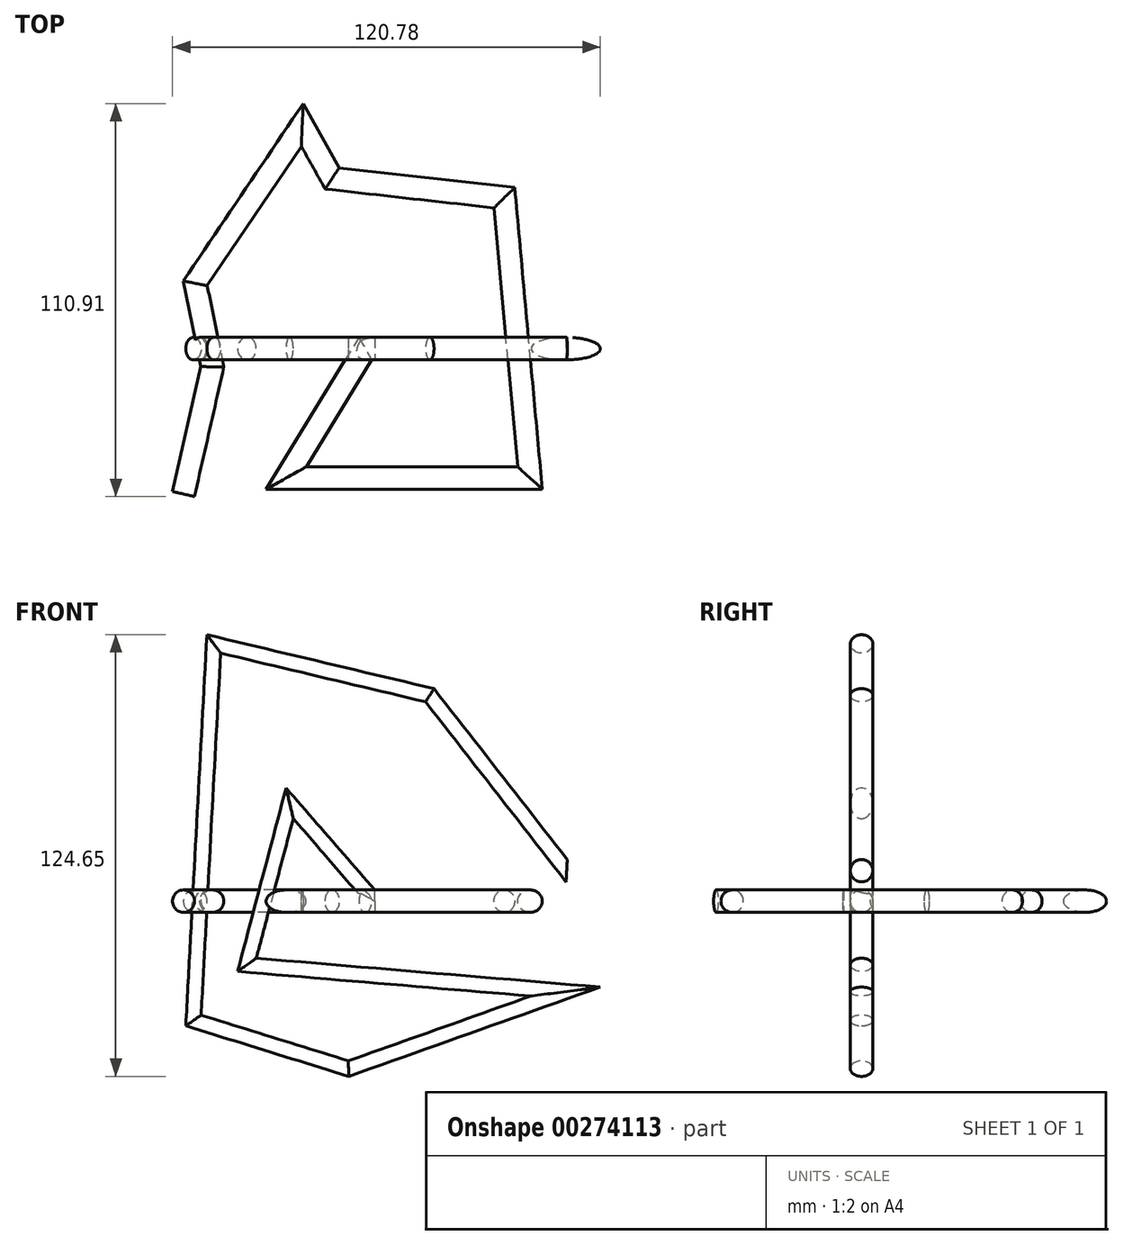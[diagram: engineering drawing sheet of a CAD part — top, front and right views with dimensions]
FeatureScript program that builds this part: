
annotation { "Feature Type Name" : "Feature", "Feature Type Description" : "" }
export const myFeature = defineFeature(function(context is Context, id is Id, definition is map)
    precondition{}
    {
        {
            var Q0;
            Q0=qCreatedBy(makeId("Top.planeOp"),FACE);
            var sketch = newSketch(context, id + "F0", { "sketchPlane" : qUnion([Q0])});
            skLineSegment(sketch, "E0", {"start": v(-2.66, 0) * mm, "end": v(-25, -36.52) * mm});
            skLineSegment(sketch, "E1", {"start": v(-25, -36.52) * mm, "end": v(43.84, -36.52) * mm});
            skLineSegment(sketch, "E2", {"start": v(43.84, -36.52) * mm, "end": v(36.6, 42.58) * mm});
            skLineSegment(sketch, "E3", {"start": v(36.6, 42.58) * mm, "end": v(-12.02, 48.02) * mm});
            skLineSegment(sketch, "E4", {"start": v(-12.02, 48.02) * mm, "end": v(-20.47, 63.11) * mm});
            skLineSegment(sketch, "E5", {"start": v(-20.47, 63.11) * mm, "end": v(-50.66, 18.43) * mm});
            skLineSegment(sketch, "E6", {"start": v(-50.66, 18.43) * mm, "end": v(-45.83, -5.12) * mm});
            skLineSegment(sketch, "E7", {"start": v(-45.83, -5.12) * mm, "end": v(-53.99, -41.05) * mm});
            skLineSegment(sketch, "E8", {"start": v(-2.66, 0) * mm, "end": v(0, 0) * mm});
            skSolve(sketch);
        }
        {
            var Q0;
            Q0=qCreatedBy(makeId("Front.planeOp"),FACE);
            var sketch = newSketch(context, id + "F1", { "sketchPlane" : qUnion([Q0])});
            skLineSegment(sketch, "E9", {"start": v(0, 0) * mm, "end": v(-24, 27.63) * mm});
            skLineSegment(sketch, "E10", {"start": v(-24, 27.63) * mm, "end": v(-36.08, -17.96) * mm});
            skLineSegment(sketch, "E11", {"start": v(-36.08, -17.96) * mm, "end": v(53.9, -25.51) * mm});
            skLineSegment(sketch, "E12", {"start": v(53.9, -25.51) * mm, "end": v(-7.4, -47.25) * mm});
            skLineSegment(sketch, "E13", {"start": v(-7.4, -47.25) * mm, "end": v(-51.18, -33.66) * mm});
            skLineSegment(sketch, "E14", {"start": v(-51.18, -33.66) * mm, "end": v(-45.44, 72.61) * mm});
            skLineSegment(sketch, "E15", {"start": v(-45.44, 72.61) * mm, "end": v(15.55, 58.12) * mm});
            skLineSegment(sketch, "E16", {"start": v(15.55, 58.12) * mm, "end": v(54.2, 8.6) * mm});
            skSolve(sketch);
        }
        {
            var Q0;
            Q0=qCreatedBy(makeId("Right.planeOp"),FACE);
            var sketch = newSketch(context, id + "F2", { "sketchPlane" : qUnion([Q0])});
            skCircle(sketch, "E17", {"center": v(0, 0) * mm, "radius": 3.18 * mm});
            skSolve(sketch);
        }
        {
            var Q0;
            Q0=makeQuery(id+"F2.imprint","IMPRINT",FACE,{"disambiguationData":[TD([[makeQuery(id+"F2.imprint","IMPRINT",EDGE,{"derivedFrom":sQuery(id+"F2.wireOp",EDGE,"E17")}),1.0]])]});
            var Q1;
            Q1=sQuery(id+"F1.wireOp",EDGE,"E9");
            var Q2;
            Q2=sQuery(id+"F1.wireOp",EDGE,"E10");
            var Q3;
            Q3=sQuery(id+"F1.wireOp",EDGE,"E11");
            var Q4;
            Q4=sQuery(id+"F1.wireOp",EDGE,"E12");
            var Q5;
            Q5=sQuery(id+"F1.wireOp",EDGE,"E13");
            var Q6;
            Q6=sQuery(id+"F1.wireOp",EDGE,"E14");
            var Q7;
            Q7=sQuery(id+"F1.wireOp",EDGE,"E15");
            var Q8;
            Q8=sQuery(id+"F1.wireOp",EDGE,"E16");
            sweep(context, id + "F3", {"profiles" : qUnion([Q0]), "path" : qUnion([Q1, Q2, Q3, Q4, Q5, Q6, Q7, Q8])});
        }
        {
            var Q0;
            Q0=makeQuery(id+"F2.imprint","IMPRINT",FACE,{"disambiguationData":[TD([[makeQuery(id+"F2.imprint","IMPRINT",EDGE,{"derivedFrom":sQuery(id+"F2.wireOp",EDGE,"E17")}),1.0]])]});
            var Q1;
            Q1=sQuery(id+"F0.wireOp",EDGE,"E8");
            var Q2;
            Q2=sQuery(id+"F0.wireOp",EDGE,"E0");
            var Q3;
            Q3=sQuery(id+"F0.wireOp",EDGE,"E1");
            var Q4;
            Q4=sQuery(id+"F0.wireOp",EDGE,"E2");
            var Q5;
            Q5=sQuery(id+"F0.wireOp",EDGE,"E3");
            var Q6;
            Q6=sQuery(id+"F0.wireOp",EDGE,"E4");
            var Q7;
            Q7=sQuery(id+"F0.wireOp",EDGE,"E5");
            var Q8;
            Q8=sQuery(id+"F0.wireOp",EDGE,"E6");
            var Q9;
            Q9=sQuery(id+"F0.wireOp",EDGE,"E7");
            sweep(context, id + "F4", {"operationType" : NewBodyOperationType.ADD, "profiles" : qUnion([Q0]), "path" : qUnion([Q1, Q2, Q3, Q4, Q5, Q6, Q7, Q8, Q9])});
        }
    });
